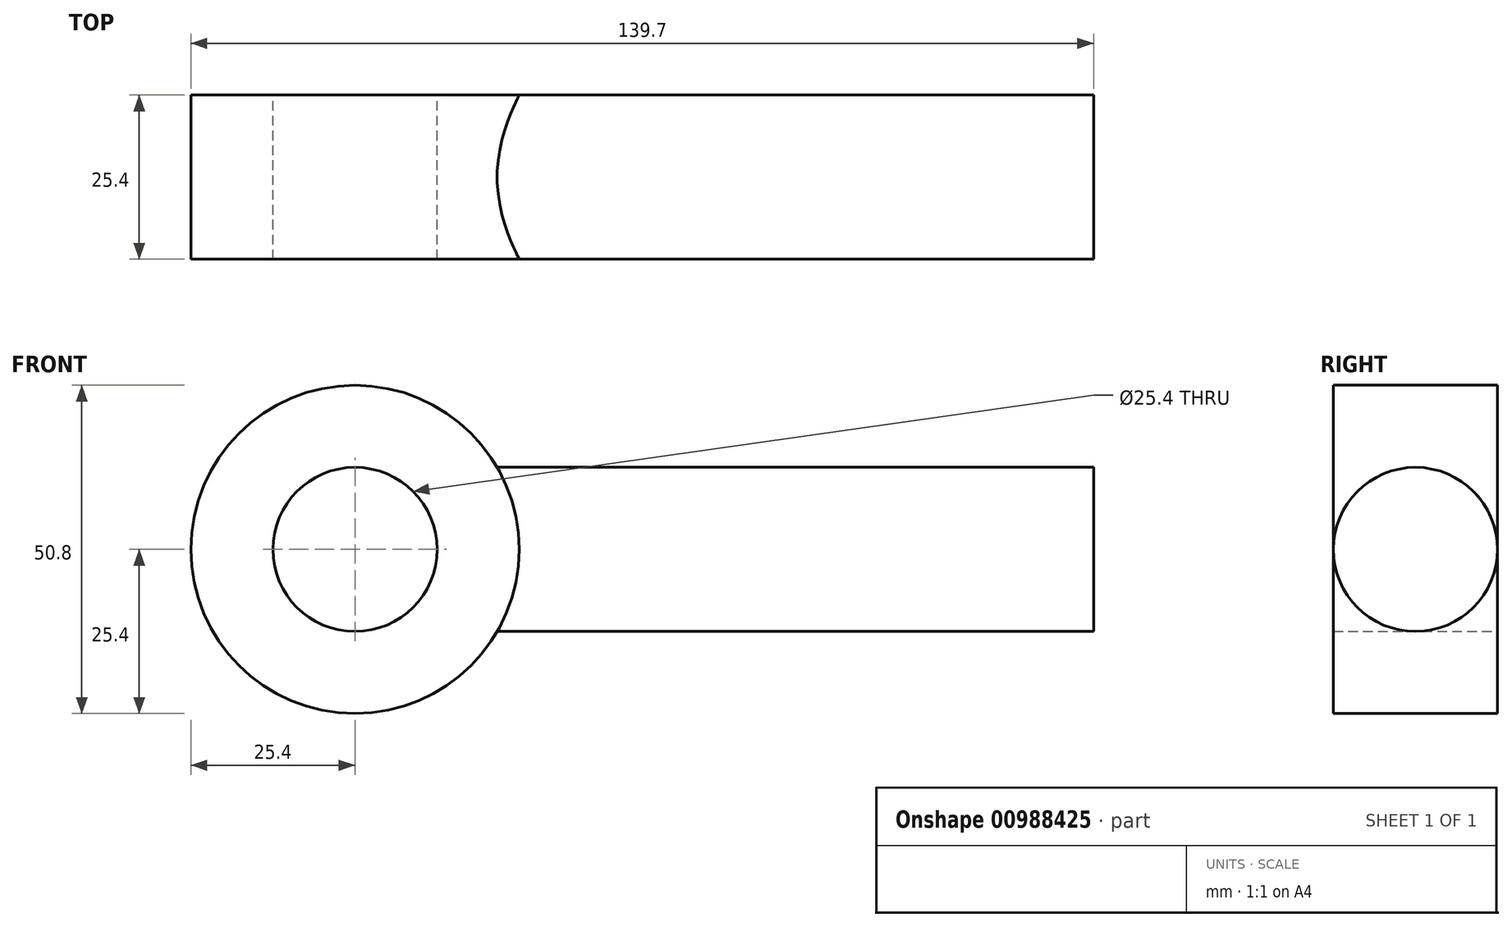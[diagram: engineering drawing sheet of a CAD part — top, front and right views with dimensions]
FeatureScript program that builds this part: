
annotation { "Feature Type Name" : "Feature", "Feature Type Description" : "" }
export const myFeature = defineFeature(function(context is Context, id is Id, definition is map)
    precondition{}
    {
        {
            assignVariable(context, id + "F0", {"name" : "FittingEyeBoltDiam", "anyValue" : 25.4 * mm});
        }
        {
            assignVariable(context, id + "F1", {"name" : "FittingEyeBoltThickness", "anyValue" : 25.4 * mm});
        }
        {
            var Q0;
            Q0=qCreatedBy(makeId("Front.planeOp"),FACE);
            var sketch = newSketch(context, id + "F2", { "sketchPlane" : qUnion([Q0])});
            skCircle(sketch, "E0", {"center": v(0, 0) * mm, "radius": 12.7 * mm});
            skCircle(sketch, "E1", {"center": v(0, 0) * mm, "radius": 25.4 * mm});
            skSolve(sketch);
        }
        {
            var Q0;
            Q0 = qSketchRegion(id + "F2", true);
            extrude(context, id + "F3", {"entities" : qUnion([Q0]), "depth" : getVariable(context, 'FittingEyeBoltThickness'), "offsetDistance" : 25.4 * mm, "symmetric" : true});
        }
        {
            var Q0;
            Q0=qCreatedBy(makeId("Right.planeOp"),FACE);
            cPlane(context, id + "F4", {"entities" : qUnion([Q0]), "cplaneType" : CPlaneType.OFFSET, "offset" : getVariable(context, 'FittingEyeBoltDiam') / 2, "width" : 152.4 * mm, "height" : 152.4 * mm});
        }
        {
            var Q0;
            Q0=qCreatedBy(id+"F4.planeOp",FACE);
            var sketch = newSketch(context, id + "F5", { "sketchPlane" : qUnion([Q0])});
            skCircle(sketch, "E2", {"center": v(0, 0) * mm, "radius": 12.7 * mm});
            skSolve(sketch);
        }
        {
            var Q0;
            Q0 = qSketchRegion(id + "F5", true);
            extrude(context, id + "F6", {"entities" : qUnion([Q0]), "operationType" : NewBodyOperationType.ADD, "depth" : 101.6 * mm, "offsetDistance" : 25.4 * mm});
        }
    });
